# Revit family: ef-30_40b(t)sxc2_d(t)sxc2-fq_60Hz
name_source: partatom
category: 機械設備
units: mm (PartAtom-declared; Revit-internal decimal feet)

## family parameters
OmniClass タイトル = Industrial Ventilating Equipment
OmniClass 番号 = 23.75.35.21.17
パーツ タイプ = 標準
ロード時にボイドで切り取り = はい
丸型コネクタ寸法 = 直径を使用
作業面ベース = いいえ
共有 = いいえ
常に垂直 = はい
部屋計算ポイント = はい

## types (6) — shared parameters
IfcExportAs = IfcFanType
IfcExportType = TUBEAXIAL
MID風量 = 0.0 m³/h
MIN風量 = 0.0 m³/h
OmniClassCode = 23-33 31 19 11 17
URL = https://www.mitsubishielectric.co.jp
Uniclass2015Code = Pr_65_67_29_67
Uniclass2015Title = Propeller fans
Uniclass2015Version = Systems v1.9
オリフィス_Depth = 45  [stored 0.147638 ft]
ファンの種類 = 軸流羽根
フレームの厚さ = 71  [stored 0.23294 ft]
ボックス_Height = 131  [stored 0.42979 ft]
レグ_Height = 413  [stored 1.35499 ft]
レグ_Width = 413  [stored 1.35499 ft]
仕様書バージョン = Version1.0
企業コード = 108420
分類コード = 50052503100110
周波数 = 60 Hz
呼称 = 有圧扇
極 = 4
法定耐用年数 = 15
製品リリース年月 = 2022年6月1日
製品出荷対象 = 国内
製造元 = 三菱電機株式会社
設置方法 = 壁付
説明 = 産業用有圧換気扇 低騒音形ステンレスタイプ オールステンレス高耐食タイプ 給気専用
負荷分類 = 3_ファン類
運転質量 = 0.00 kg

## per-type parameters (varying)
| type | Box_H | Box_W | Depth | Height | MAX風量 | Width | オリフィス径 | ボックス_Depth | ボックス_Width | モデル | モーター径 | レグ_Depth | 価格 | 極数 | 消費電力 | 相 | 羽根径 | 製品質量 | 質量 | 電動機出力 | 電圧 |
| EF-30BSXC2-FQ | 108 | 162  [stored 0.531496 ft] | 224  [stored 0.734908 ft] | 420  [stored 1.37795 ft] | 1980.0 m³/h | 420  [stored 1.37795 ft] | 348  [stored 1.14173 ft] | 106 | 46 | EF-30BSXC2-FQ | 99  [stored 0.324803 ft] | 208 | 283000 $ | 2 | 73 W | 1 | ∅300 | 7.00 kg | 8.40 kg | 50 W | 100 V |
| EF-40DSXC2-FQ | 185 | 213 | 286 | 520  [stored 1.70604 ft] | 4360.0 m³/h | 520  [stored 1.70604 ft] | 476  [stored 1.56168 ft] | 119 | 47 | EF-40DSXC2-FQ | 113  [stored 0.370735 ft] | 250  [stored 0.82021 ft] | 348000 $ | 2 | 195 W | 1 | ∅400 | 15.00 kg | 18.00 kg | 200 W | 100 V |
| EF-30BTXC2-FQ_200V | 108 | 162  [stored 0.531496 ft] | 224  [stored 0.734908 ft] | 420  [stored 1.37795 ft] | 1980.0 m³/h | 420  [stored 1.37795 ft] | 348  [stored 1.14173 ft] | 106 | 46 | EF-30BTXC2-FQ | 99  [stored 0.324803 ft] | 208 | 283000 $ | 3 | 65 W | 3 | ∅300 | 7.50 kg | 9.00 kg | 50 W | 200 V |
| EF-40DTXC2-FQ_200V | 185 | 213 | 286 | 520  [stored 1.70604 ft] | 4360.0 m³/h | 520  [stored 1.70604 ft] | 476  [stored 1.56168 ft] | 119 | 47 | EF-40DTXC2-FQ | 113  [stored 0.370735 ft] | 250  [stored 0.82021 ft] | 348000 $ | 3 | 177 W | 3 | ∅400 | 15.00 kg | 18.00 kg | 200 W | 200 V |
| EF-30BTXC2-FQ_220V | 108 | 162  [stored 0.531496 ft] | 224  [stored 0.734908 ft] | 420  [stored 1.37795 ft] | 1980.0 m³/h | 420  [stored 1.37795 ft] | 348  [stored 1.14173 ft] | 106 | 46 | EF-30BTXC2-FQ | 99  [stored 0.324803 ft] | 208 | 283000 $ | 3 | 71 W | 3 | ∅300 | 7.50 kg | 9.00 kg | 50 W | 220 V |
| EF-40DTXC2-FQ_220V | 185 | 213 | 286 | 520  [stored 1.70604 ft] | 4360.0 m³/h | 520  [stored 1.70604 ft] | 476  [stored 1.56168 ft] | 119 | 47 | EF-40DTXC2-FQ | 113  [stored 0.370735 ft] | 250  [stored 0.82021 ft] | 348000 $ | 3 | 188 W | 3 | ∅400 | 15.00 kg | 18.00 kg | 200 W | 220 V |

note: [stored X ft] marks values corroborated as IEEE doubles in the binary element streams (Revit-internal decimal feet)
